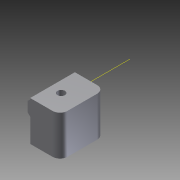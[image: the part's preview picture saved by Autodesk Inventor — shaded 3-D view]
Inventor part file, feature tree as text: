
AUTODESK INVENTOR PART (.ipt)
format: ipt  version: 2012 (Build 160160000, 160)  size: 119,808 bytes
history: native  units: mm
features: hole x3, extrude x2, sketch x2, chamfer x1, fillet x1, other x1, plane x1, mirror x1
ambient origin geometry x8: Origin, YZ Plane, XZ Plane, XY Plane, X Axis, Y Axis, Z Axis, Center Point
bodies: Solid1 (feature_tree)
feature tree (12):
  extrude  "Extrusion1"  Depth=9.5mm
  extrude  "Extrusion2"  Depth=12.0mm
  hole  "Hole1"  [1 undecoded]
  chamfer  "Chamfer1"  Distance=8.0mm
  fillet  "Fillet1"  Radius=4.0mm
  hole  "Hole2"  [1 undecoded]
  other  "Work Axis1"
  plane  "Work Plane1"
  mirror  "Mirror1"
  hole  "Hole4"  [1 undecoded]
  sketch  "Sketch1"  dims[d0=9.5mm d1=9.5mm]
  sketch  "Sketch2"  dims[d2=18.0mm d3=12.0mm d4=8.0mm d5=0.0mm d6=8.0mm d7=0.0mm d8=4.0mm d9=4.0mm d10=3.0mm d11=6.0mm d12=4.0mm d13=2.0mm d14=90.0deg d15=8.0mm d16=20.594885mm d17=2.0mm d18=2.0mm d19=45.0deg d20=3.0mm d21=8.0mm d22=4.5mm d23=3.0mm d24=6.0mm d25=4.0mm d26=2.0mm d27=90.0deg d28=8.0mm d29=20.594885mm d39=5.0mm d49=10.0mm d50=10.0mm d42=6.0mm d43=6.0mm d44=4.0mm d45=2.0mm d46=90.0deg d47=2.0mm d48=0.0mm]
note: 3 required parameter values undecoded (feature->parameter linkage not recoverable at this tier; creation-order binding heuristic only, values carry confidence <= 0.55)
